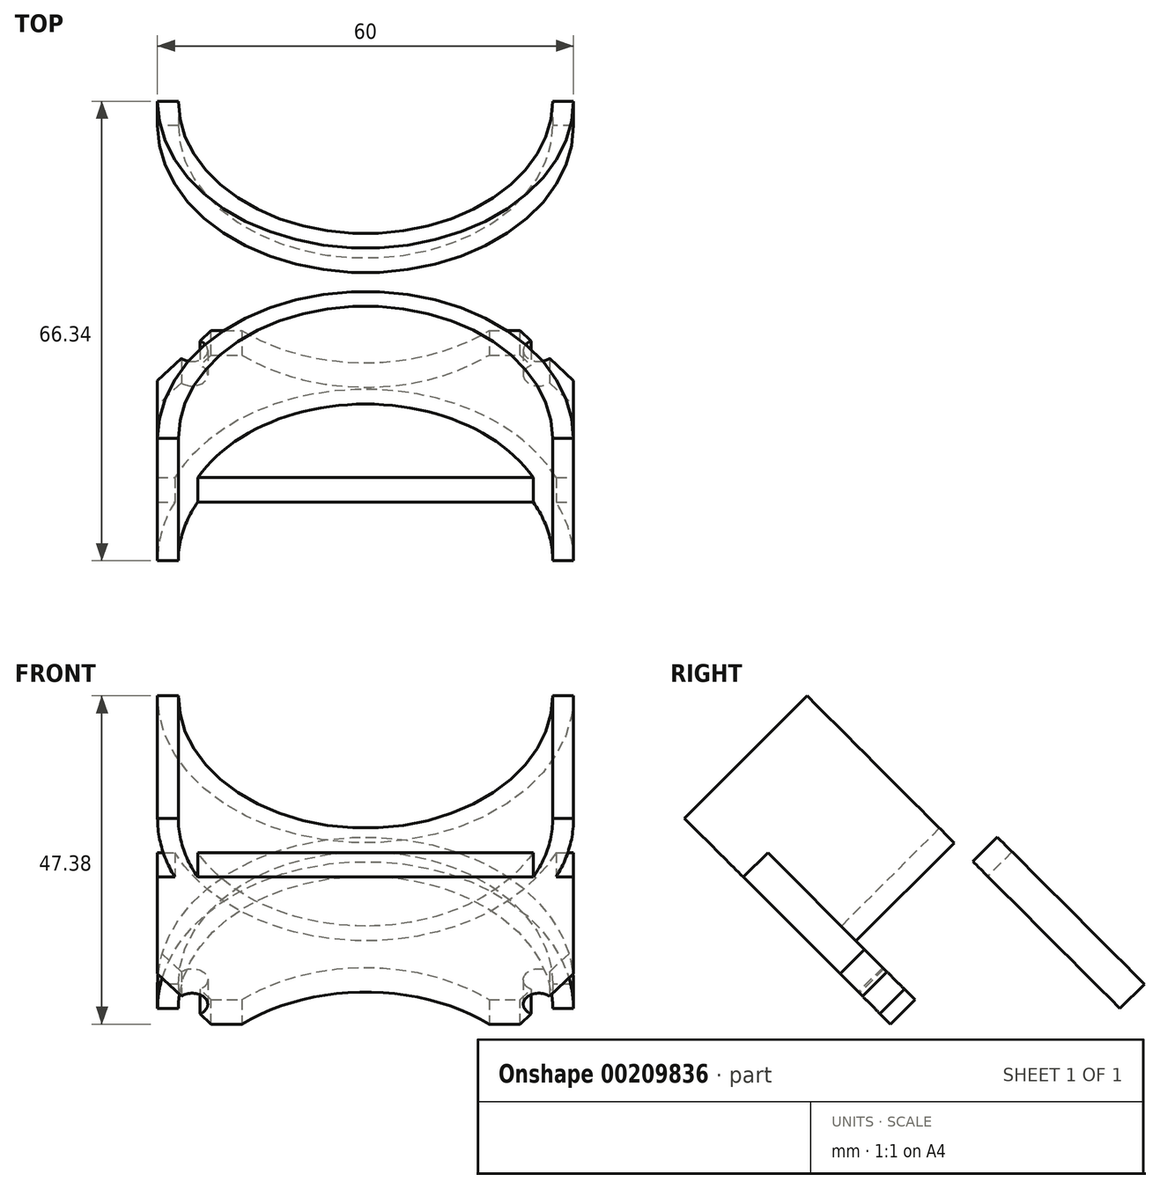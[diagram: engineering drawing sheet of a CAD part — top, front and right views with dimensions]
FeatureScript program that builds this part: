
annotation { "Feature Type Name" : "Feature", "Feature Type Description" : "" }
export const myFeature = defineFeature(function(context is Context, id is Id, definition is map)
    precondition{}
    {
        {
            var Q0;
            Q0=qCreatedBy(makeId("Top.planeOp"),FACE);
            var sketch = newSketch(context, id + "F0", { "sketchPlane" : qUnion([Q0])});
            skLineSegment(sketch, "E0.bottom", {"start": v(-30, 9.76) * mm, "end": v(-17.82, 9.76) * mm});
            skLineSegment(sketch, "E0.top", {"start": v(-30, -5.24) * mm, "end": v(30, -5.24) * mm});
            skLineSegment(sketch, "E0.left", {"start": v(-30, 9.76) * mm, "end": v(-30, -5.24) * mm});
            skLineSegment(sketch, "E0.right", {"start": v(30, 9.76) * mm, "end": v(30, -5.24) * mm});
            skCircle(sketch, "E1", {"center": v(-25, 5.7) * mm, "radius": 2.25 * mm});
            skCircle(sketch, "E2", {"center": v(25, 5.7) * mm, "radius": 2.25 * mm});
            skArc(sketch, "E3", {"start": v(-17.82, 9.76) * mm, "mid": v(0, 3.2) * mm, "end": v(17.82, 9.76) * mm});
            skLineSegment(sketch, "E4.trimOffspring", {"start": v(17.82, 9.76) * mm, "end": v(30, 9.76) * mm});
            skSolve(sketch);
        }
        {
            var Q0;
            Q0 = qSketchRegion(id + "F0", true);
            extrude(context, id + "F1", {"entities" : qUnion([Q0]), "depth" : 5 * mm});
        }
        {
            var Q0;
            Q0=qCreatedBy(makeId("Top.planeOp"),FACE);
            var sketch = newSketch(context, id + "F2", { "sketchPlane" : qUnion([Q0])});
            skArc(sketch, "E5", {"start": v(27, -32.24) * mm, "mid": v(0, -5.24) * mm, "end": v(-27, -32.24) * mm});
            skArc(sketch, "E6.0", {"start": v(30, -32.24) * mm, "mid": v(0, -2.24) * mm, "end": v(-30, -32.24) * mm});
            skLineSegment(sketch, "E7", {"start": v(-27, -32.24) * mm, "end": v(-30, -32.24) * mm});
            skLineSegment(sketch, "E8", {"start": v(27, -32.24) * mm, "end": v(30, -32.24) * mm});
            skLineSegment(sketch, "E9.0.0", {"start": v(30, -5.24) * mm, "end": v(30, 9.76) * mm, "construction": true});
            skLineSegment(sketch, "E9.0.1", {"start": v(30, 9.76) * mm, "end": v(17.82, 9.76) * mm, "construction": true});
            skArc(sketch, "E9.0.2", {"start": v(17.82, 9.76) * mm, "mid": v(0, 3.2) * mm, "end": v(-17.82, 9.76) * mm, "construction": true});
            skLineSegment(sketch, "E9.0.3", {"start": v(-17.82, 9.76) * mm, "end": v(-30, 9.76) * mm, "construction": true});
            skLineSegment(sketch, "E9.0.4", {"start": v(-30, 9.76) * mm, "end": v(-30, -5.24) * mm, "construction": true});
            skLineSegment(sketch, "E9.0.5", {"start": v(-30, -5.24) * mm, "end": v(30, -5.24) * mm, "construction": true});
            skSolve(sketch);
        }
        {
            var Q0;
            Q0 = qSketchRegion(id + "F2", true);
            extrude(context, id + "F3", {"entities" : qUnion([Q0]), "depth" : 25 * mm});
        }
        {
            var Q0;
            Q0=makeQuery(id+"F1.opExtrude","SWEPT_FACE",FACE,{"disambiguationData":[OSD([sQuery(id+"F0.wireOp",EDGE,"E0.top")])]});
            var sketch = newSketch(context, id + "F4", { "sketchPlane" : qUnion([Q0])});
            skLineSegment(sketch, "E10.0.0", {"start": v(-30, 0) * mm, "end": v(30, 0) * mm});
            skLineSegment(sketch, "E10.0.1", {"start": v(30, 0) * mm, "end": v(30, 5) * mm});
            skLineSegment(sketch, "E10.0.2", {"start": v(30, 5) * mm, "end": v(-30, 5) * mm});
            skLineSegment(sketch, "E10.0.3", {"start": v(-30, 5) * mm, "end": v(-30, 0) * mm});
            skSolve(sketch);
        }
        {
            var Q0;
            Q0 = qSketchRegion(id + "F4", true);
            extrude(context, id + "F5", {"entities" : qUnion([Q0]), "operationType" : NewBodyOperationType.ADD, "depth" : 15 * mm});
        }
        {
            var Q0;
            Q0=makeQuery(id+"F5.boolean.opBoolean","MERGE",FACE,{"derivedFrom":[makeQuery(id+"F1.opExtrude","CAP_FACE",FACE,{"disambiguationData":[OSD([sQuery(id+"F0.wireOp",EDGE,"E0.bottom"),sQuery(id+"F0.wireOp",EDGE,"E0.top"),sQuery(id+"F0.wireOp",EDGE,"E0.left"),sQuery(id+"F0.wireOp",EDGE,"E0.right"),sQuery(id+"F0.wireOp",EDGE,"E1"),sQuery(id+"F0.wireOp",EDGE,"E2"),sQuery(id+"F0.wireOp",EDGE,"E3"),sQuery(id+"F0.wireOp",EDGE,"E4.trimOffspring")])],"isStart":true}),makeQuery(id+"F5.opExtrude","SWEPT_FACE",FACE,{"disambiguationData":[OSD([sQuery(id+"F4.wireOp",EDGE,"E10.0.0")])]})]});
            var sketch = newSketch(context, id + "F6", { "sketchPlane" : qUnion([Q0])});
            skArc(sketch, "E11.0", {"start": v(30, 32.24) * mm, "mid": v(0, 2.24) * mm, "end": v(-30, 32.24) * mm, "construction": true});
            skLineSegment(sketch, "E12", {"start": v(0, 2.24) * mm, "end": v(-49.4, 2.24) * mm});
            skSolve(sketch);
        }
        {
            var Q0;
            Q0=makeQuery(id+"F1.opExtrude","SWEPT_BODY",BODY,{"disambiguationData":[OSD([sQuery(id+"F0.wireOp",EDGE,"E0.bottom"),sQuery(id+"F0.wireOp",EDGE,"E0.top"),sQuery(id+"F0.wireOp",EDGE,"E0.left"),sQuery(id+"F0.wireOp",EDGE,"E0.right"),sQuery(id+"F0.wireOp",EDGE,"E1"),sQuery(id+"F0.wireOp",EDGE,"E2"),sQuery(id+"F0.wireOp",EDGE,"E3"),sQuery(id+"F0.wireOp",EDGE,"E4.trimOffspring")])]});
            var Q1;
            Q1=sQuery(id+"F6.wireOp",EDGE,"E12");
            transform(context, id + "F7", {"entities" : qUnion([Q0]), "transformType" : TransformType.ROTATION, "transformAxis" : qUnion([Q1]), "angle" : 45 * degree, "makeCopy" : false});
        }
        {
            var Q0;
            Q0=makeQuery(id+"F3.opExtrude","CAP_FACE",FACE,{"disambiguationData":[OSD([sQuery(id+"F2.wireOp",EDGE,"E5"),sQuery(id+"F2.wireOp",EDGE,"E6.0"),sQuery(id+"F2.wireOp",EDGE,"E7"),sQuery(id+"F2.wireOp",EDGE,"E8")])],"isStart":false});
            var sketch = newSketch(context, id + "F8", { "sketchPlane" : qUnion([Q0])});
            skArc(sketch, "E13.0", {"start": v(27, -32.24) * mm, "mid": v(0, -5.24) * mm, "end": v(-27, -32.24) * mm});
            skLineSegment(sketch, "E14", {"start": v(-27, -32.24) * mm, "end": v(27, -32.24) * mm});
            skSolve(sketch);
        }
        {
            var Q0;
            Q0 = qSketchRegion(id + "F8", true);
            extrude(context, id + "F9", {"entities" : qUnion([Q0]), "operationType" : NewBodyOperationType.REMOVE, "oppositeDirection" : true, "depth" : 25 * mm});
        }
        {
            var Q0;
            Q0=makeQuery(id+"F3.opExtrude","CAP_FACE",FACE,{"disambiguationData":[OSD([sQuery(id+"F2.wireOp",EDGE,"E5"),sQuery(id+"F2.wireOp",EDGE,"E6.0"),sQuery(id+"F2.wireOp",EDGE,"E7"),sQuery(id+"F2.wireOp",EDGE,"E8")])],"isStart":false});
            var sketch = newSketch(context, id + "F10", { "sketchPlane" : qUnion([Q0])});
            skArc(sketch, "E15.0", {"start": v(-21.56, -11.38) * mm, "mid": v(-27.81, -20.99) * mm, "end": v(-30, -32.24) * mm});
            skLineSegment(sketch, "E16", {"start": v(-21.56, -11.38) * mm, "end": v(-30.12, 0) * mm});
            skLineSegment(sketch, "E17", {"start": v(-30.12, 0) * mm, "end": v(-30, -32.24) * mm});
            skLineSegment(sketch, "E18", {"start": v(0, -32.24) * mm, "end": v(0, -13.64) * mm, "construction": true});
            skPoint(sketch, "E19.orphan", {"position": v(30, -32.24) * mm});
            skLineSegment(sketch, "E20.MirrorCS", {"start": v(30.12, 0) * mm, "end": v(30, -32.24) * mm});
            skLineSegment(sketch, "E21.MirrorCS", {"start": v(21.56, -11.38) * mm, "end": v(30.12, 0) * mm});
            skArc(sketch, "E22.MirrorCS", {"start": v(21.56, -11.38) * mm, "mid": v(27.81, -20.99) * mm, "end": v(30, -32.24) * mm});
            skSolve(sketch);
        }
        {
            var Q0;
            Q0 = qSketchRegion(id + "F10", true);
            extrude(context, id + "F11", {"entities" : qUnion([Q0]), "operationType" : NewBodyOperationType.REMOVE, "oppositeDirection" : true, "depth" : 29.2 * mm});
        }
        {
            var Q0;
            Q0=qCreatedBy(makeId("Right.planeOp"),FACE);
            var sketch = newSketch(context, id + "F12", { "sketchPlane" : qUnion([Q0])});
            skLineSegment(sketch, "E23.0", {"start": v(-11.38, 9.14) * mm, "end": v(-2.24, 0) * mm});
            skLineSegment(sketch, "E24.0", {"start": v(-32.24, 9.14) * mm, "end": v(-32.24, 0) * mm});
            skLineSegment(sketch, "E25", {"start": v(-11.38, 9.14) * mm, "end": v(-32.24, 9.14) * mm});
            skLineSegment(sketch, "E26", {"start": v(-32.24, 0) * mm, "end": v(-2.24, 0) * mm});
            skPoint(sketch, "E27.orphan", {"position": v(-0.16, -2.08) * mm});
            skPoint(sketch, "E28.orphan", {"position": v(-32.24, 25) * mm});
            skSolve(sketch);
        }
        {
            var Q0;
            Q0 = qSketchRegion(id + "F12", true);
            extrude(context, id + "F13", {"entities" : qUnion([Q0]), "operationType" : NewBodyOperationType.REMOVE, "oppositeDirection" : true, "depth" : 84.4 * mm, "symmetric" : true});
        }
        {
            var Q0;
            Q0=makeQuery(id+"F3.opExtrude","CAP_FACE",FACE,{"disambiguationData":[OSD([sQuery(id+"F2.wireOp",EDGE,"E5"),sQuery(id+"F2.wireOp",EDGE,"E6.0"),sQuery(id+"F2.wireOp",EDGE,"E7"),sQuery(id+"F2.wireOp",EDGE,"E8")])],"isStart":false});
            var sketch = newSketch(context, id + "F14", { "sketchPlane" : qUnion([Q0])});
            skLineSegment(sketch, "E29.0.0", {"start": v(27, -32.24) * mm, "end": v(30, -32.24) * mm});
            skArc(sketch, "E29.0.1", {"start": v(30, -32.24) * mm, "mid": v(0, -2.24) * mm, "end": v(-30, -32.24) * mm});
            skLineSegment(sketch, "E29.0.2", {"start": v(-30, -32.24) * mm, "end": v(-27, -32.24) * mm});
            skArc(sketch, "E29.0.3", {"start": v(-27, -32.24) * mm, "mid": v(0, -5.24) * mm, "end": v(27, -32.24) * mm});
            skSolve(sketch);
        }
        {
            var Q0;
            Q0 = qSketchRegion(id + "F14", true);
            extrude(context, id + "F15", {"entities" : qUnion([Q0]), "operationType" : NewBodyOperationType.ADD, "depth" : 5 * mm});
        }
    });
